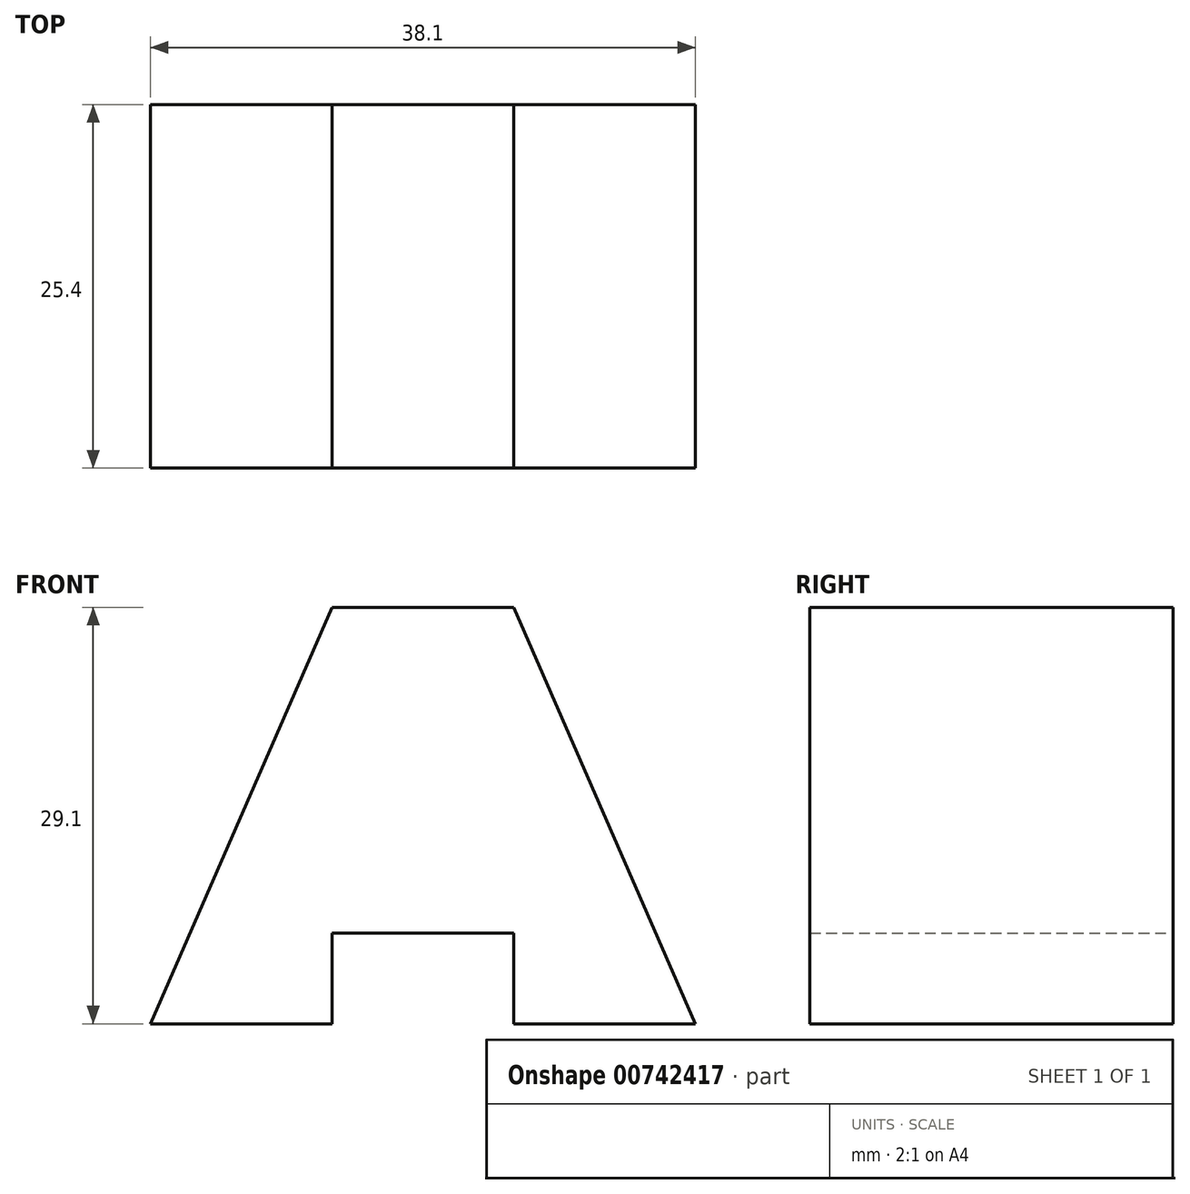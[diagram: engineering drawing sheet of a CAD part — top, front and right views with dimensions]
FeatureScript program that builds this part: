
annotation { "Feature Type Name" : "Feature", "Feature Type Description" : "" }
export const myFeature = defineFeature(function(context is Context, id is Id, definition is map)
    precondition{}
    {
        {
            var Q0;
            Q0=qCreatedBy(makeId("Front.planeOp"),FACE);
            var sketch = newSketch(context, id + "F0", { "sketchPlane" : qUnion([Q0])});
            skLineSegment(sketch, "E0", {"start": v(-20.05, 0) * mm, "end": v(-7.35, 29.1) * mm});
            skLineSegment(sketch, "E1", {"start": v(-7.35, 29.1) * mm, "end": v(5.35, 29.1) * mm});
            skLineSegment(sketch, "E2", {"start": v(5.35, 29.1) * mm, "end": v(18.05, 0) * mm});
            skLineSegment(sketch, "E3", {"start": v(-20.05, 0) * mm, "end": v(-7.35, 0) * mm});
            skLineSegment(sketch, "E4", {"start": v(-7.35, 0) * mm, "end": v(-7.35, 6.35) * mm});
            skLineSegment(sketch, "E5", {"start": v(-7.35, 6.35) * mm, "end": v(5.35, 6.35) * mm});
            skLineSegment(sketch, "E6", {"start": v(5.35, 6.35) * mm, "end": v(5.35, 0) * mm});
            skLineSegment(sketch, "E7", {"start": v(5.35, 0) * mm, "end": v(18.05, 0) * mm});
            skSolve(sketch);
        }
        {
            var Q0;
            Q0 = qSketchRegion(id + "F0", true);
            extrude(context, id + "F1", {"entities" : qUnion([Q0]), "depth" : 25.4 * mm, "offsetDistance" : 25.4 * mm});
        }
    });
